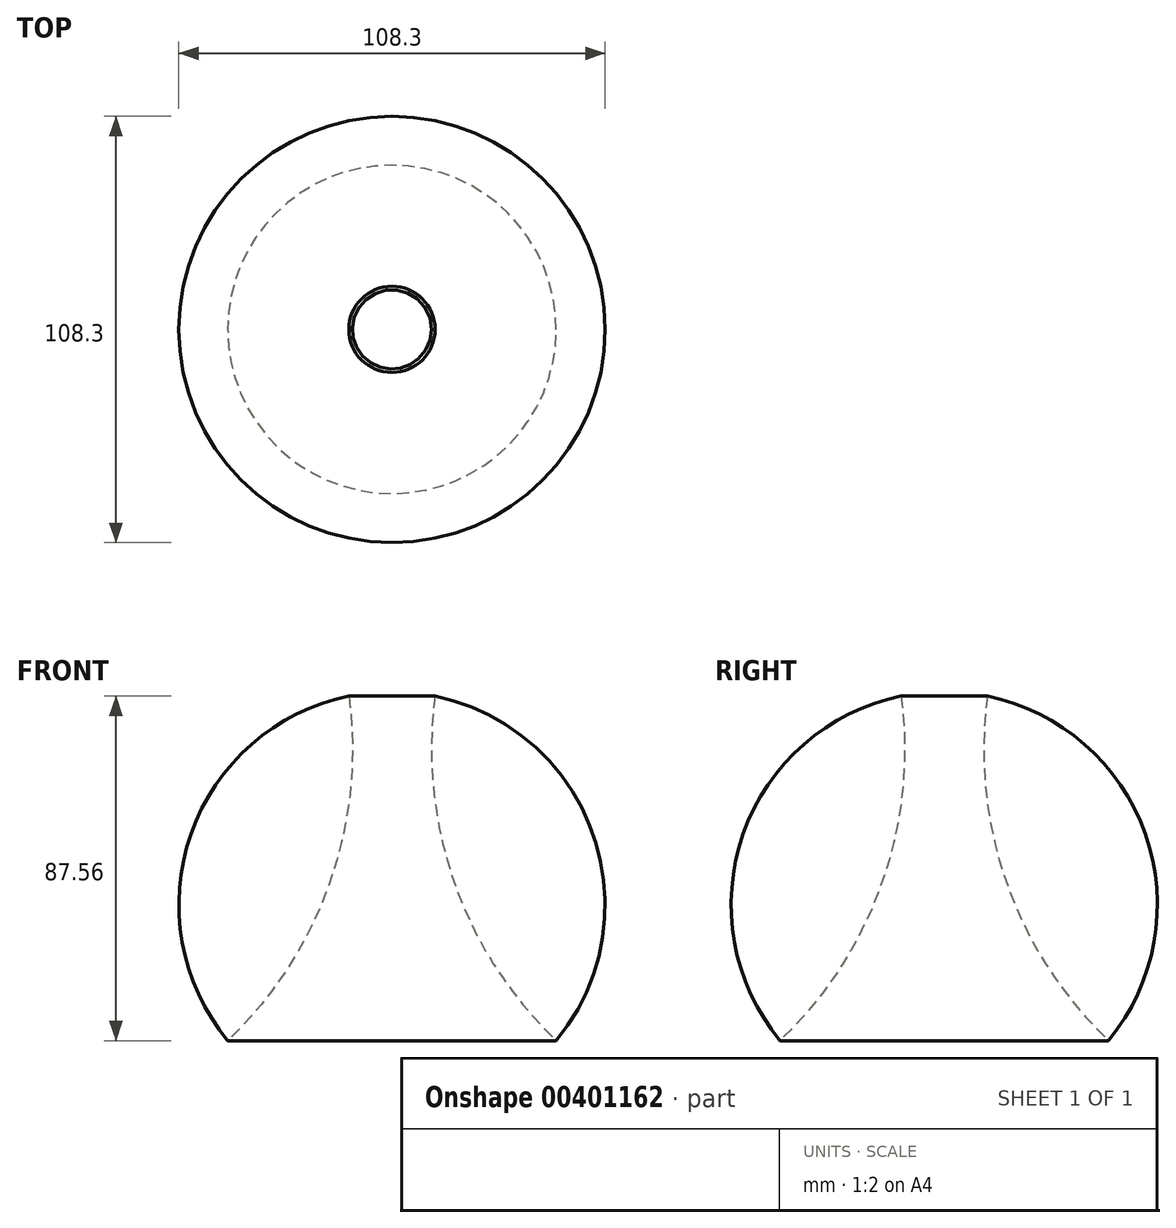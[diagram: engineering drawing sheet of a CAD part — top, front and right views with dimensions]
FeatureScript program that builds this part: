
annotation { "Feature Type Name" : "Feature", "Feature Type Description" : "" }
export const myFeature = defineFeature(function(context is Context, id is Id, definition is map)
    precondition{}
    {
        {
            var Q0;
            Q0=qCreatedBy(makeId("Front.planeOp"),FACE);
            var sketch = newSketch(context, id + "F0", { "sketchPlane" : qUnion([Q0])});
            skArc(sketch, "E0", {"start": v(-10.95, 53.03) * mm, "mid": v(-51.09, 17.95) * mm, "end": v(-41.71, -34.53) * mm});
            skArc(sketch, "E1", {"start": v(-41.71, -34.53) * mm, "mid": v(-15.84, 5.57) * mm, "end": v(-10.95, 53.03) * mm});
            skPoint(sketch, "E1.first.point", {"position": v(-41.71, -34.53) * mm});
            skPoint(sketch, "E1.second.point", {"position": v(-15.96, 5.24) * mm});
            skPoint(sketch, "E1.third.point", {"position": v(-10.95, 53.03) * mm});
            skLineSegment(sketch, "E2", {"start": v(0, 64.09) * mm, "end": v(0, -66.08) * mm, "construction": true});
            skSolve(sketch);
        }
        {
            var Q0;
            Q0 = qSketchRegion(id + "F0", true);
            var Q1;
            Q1=sQuery(id+"F0.wireOp",EDGE,"E2");
            revolve(context, id + "F1", {"entities" : qUnion([Q0]), "axis" : qUnion([Q1]), "revolveType" : RevolveType.FULL});
        }
    });
